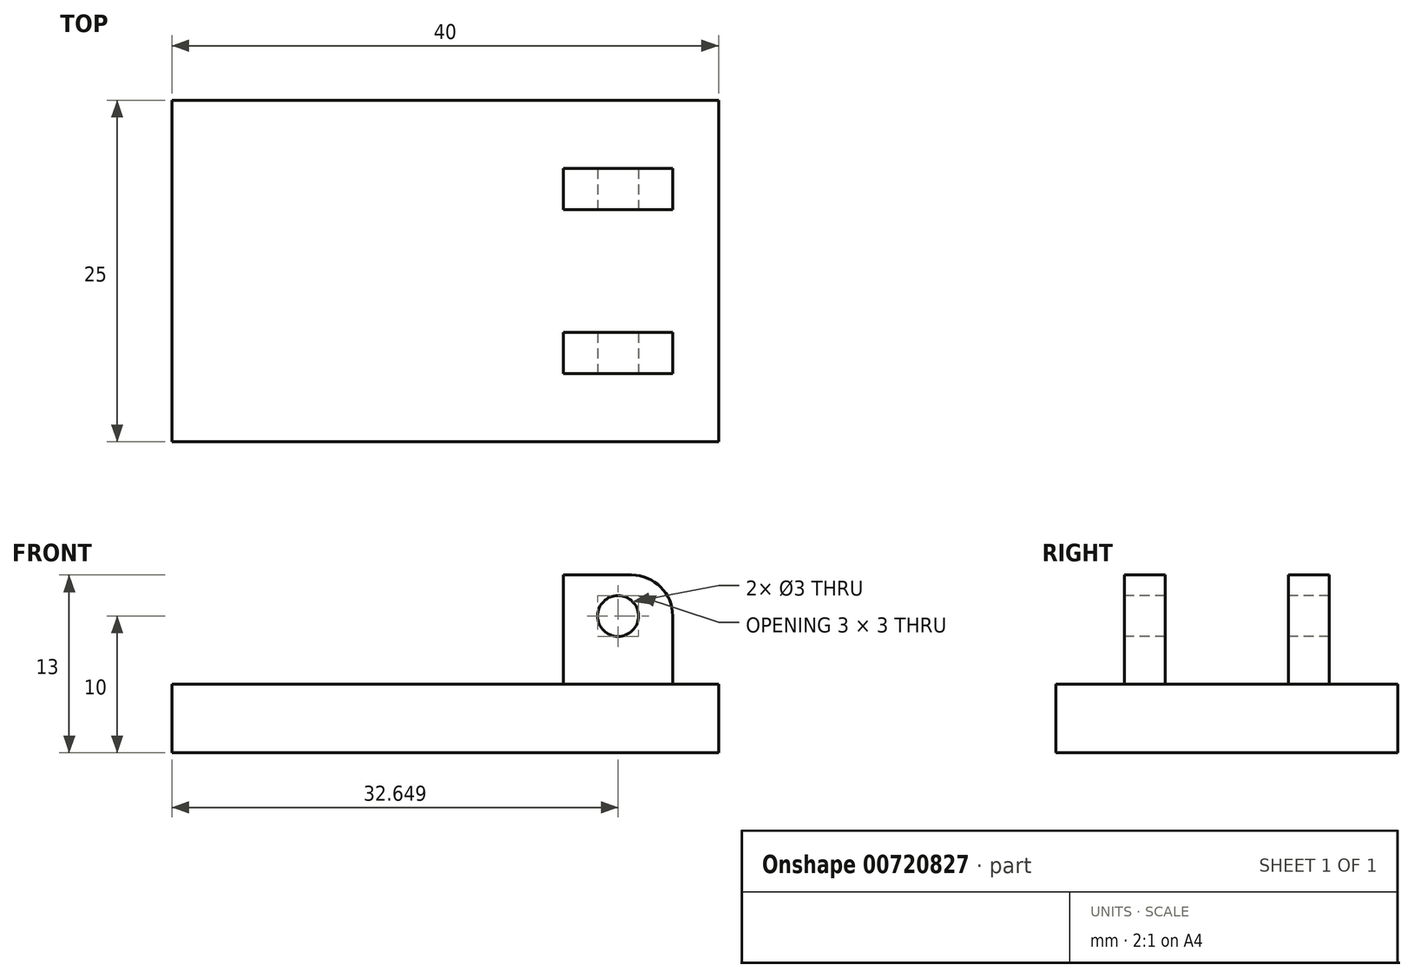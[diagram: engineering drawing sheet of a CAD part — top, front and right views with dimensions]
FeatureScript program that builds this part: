
annotation { "Feature Type Name" : "Feature", "Feature Type Description" : "" }
export const myFeature = defineFeature(function(context is Context, id is Id, definition is map)
    precondition{}
    {
        {
            var Q0;
            Q0=qCreatedBy(makeId("Top.planeOp"),FACE);
            var sketch = newSketch(context, id + "F0", { "sketchPlane" : qUnion([Q0])});
            skLineSegment(sketch, "E0.bottom", {"start": v(20, -12.5) * mm, "end": v(-20, -12.5) * mm});
            skLineSegment(sketch, "E0.top", {"start": v(20, 12.5) * mm, "end": v(-20, 12.5) * mm});
            skLineSegment(sketch, "E0.left", {"start": v(20, -12.5) * mm, "end": v(20, 12.5) * mm});
            skLineSegment(sketch, "E0.right", {"start": v(-20, -12.5) * mm, "end": v(-20, 12.5) * mm});
            skPoint(sketch, "E0.middle", {"position": v(0, 0) * mm});
            skSolve(sketch);
        }
        {
            var Q0;
            Q0=makeQuery(id+"F0.imprint","IMPRINT",FACE,{"disambiguationData":[TD([[makeQuery(id+"F0.imprint","IMPRINT",EDGE,{"derivedFrom":sQuery(id+"F0.wireOp",EDGE,"E0.bottom")}),-1.0]])]});
            extrude(context, id + "F1", {"entities" : qUnion([Q0]), "depth" : 5 * mm, "offsetDistance" : 25 * mm});
        }
        {
            var Q0;
            Q0=makeQuery(id+"F1.opExtrude","CAP_FACE",FACE,{"disambiguationData":[OSD([sQuery(id+"F0.wireOp",EDGE,"E0.bottom"),sQuery(id+"F0.wireOp",EDGE,"E0.top"),sQuery(id+"F0.wireOp",EDGE,"E0.left"),sQuery(id+"F0.wireOp",EDGE,"E0.right")])],"isStart":false});
            var sketch = newSketch(context, id + "F2", { "sketchPlane" : qUnion([Q0])});
            skLineSegment(sketch, "E1.bottom", {"start": v(16.65, -7.5) * mm, "end": v(8.65, -7.5) * mm});
            skLineSegment(sketch, "E1.top", {"start": v(16.65, 7.5) * mm, "end": v(8.65, 7.5) * mm});
            skLineSegment(sketch, "E1.right", {"start": v(8.65, -7.5) * mm, "end": v(8.65, 7.5) * mm});
            skPoint(sketch, "E1.middle", {"position": v(12.65, 0) * mm});
            skLineSegment(sketch, "E2", {"start": v(8.65, 7.5) * mm, "end": v(8.65, 4.5) * mm});
            skLineSegment(sketch, "E3", {"start": v(8.65, 4.5) * mm, "end": v(8.65, 1.5) * mm});
            skLineSegment(sketch, "E4", {"start": v(8.65, 1.5) * mm, "end": v(8.65, -1.5) * mm});
            skLineSegment(sketch, "E5", {"start": v(8.65, -1.5) * mm, "end": v(8.65, -4.5) * mm});
            skLineSegment(sketch, "E6", {"start": v(8.65, -4.5) * mm, "end": v(8.65, -7.5) * mm});
            skLineSegment(sketch, "E7", {"start": v(8.65, -7.5) * mm, "end": v(8.65, -4.5) * mm});
            skLineSegment(sketch, "E8", {"start": v(8.65, 4.5) * mm, "end": v(16.65, 4.5) * mm});
            skLineSegment(sketch, "E9", {"start": v(16.65, 4.5) * mm, "end": v(16.65, 1.5) * mm});
            skLineSegment(sketch, "E10", {"start": v(8.65, 1.5) * mm, "end": v(16.65, 1.5) * mm});
            skLineSegment(sketch, "E11", {"start": v(16.65, 1.5) * mm, "end": v(16.65, -1.5) * mm});
            skLineSegment(sketch, "E12", {"start": v(16.65, -1.5) * mm, "end": v(8.65, -1.5) * mm});
            skLineSegment(sketch, "E13.trimOffspring", {"start": v(16.65, -1.5) * mm, "end": v(16.65, 7.5) * mm});
            skLineSegment(sketch, "E14", {"start": v(16.65, -1.5) * mm, "end": v(16.65, -4.5) * mm});
            skLineSegment(sketch, "E15", {"start": v(16.65, -4.5) * mm, "end": v(16.65, -7.5) * mm});
            skLineSegment(sketch, "E16", {"start": v(8.65, -4.5) * mm, "end": v(16.65, -4.5) * mm});
            skSolve(sketch);
        }
        {
            var Q0;
            {var subQ0=sQuery(id+"F2.wireOp",EDGE,"E1.top");Q0=makeQuery(id+"F2.imprint","IMPRINT",FACE,{"disambiguationData":[TD([[makeQuery(id+"F2.imprint","IMPRINT",EDGE,{"derivedFrom":subQ0}),1.0]])]});}
            var Q1;
            Q1=makeQuery(id+"F2.imprint","IMPRINT",FACE,{"disambiguationData":[TD([[makeQuery(id+"F2.imprint","IMPRINT",EDGE,{"derivedFrom":sQuery(id+"F2.wireOp",EDGE,"E4")}),1.0]])]});
            var Q2;
            Q2=makeQuery(id+"F2.imprint","IMPRINT",FACE,{"disambiguationData":[TD([[makeQuery(id+"F2.imprint","IMPRINT",EDGE,{"derivedFrom":sQuery(id+"F2.wireOp",EDGE,"E1.bottom")}),-1.0]])]});
            extrude(context, id + "F3", {"entities" : qUnion([Q0, Q1, Q2]), "operationType" : NewBodyOperationType.ADD, "depth" : 8 * mm, "offsetDistance" : 25 * mm});
        }
        {
            var Q0;
            Q0=makeQuery(id+"F3.opExtrude","CAP_EDGE",EDGE,{"disambiguationData":[OSD([sQuery(id+"F2.wireOp",EDGE,"E7")])],"isStart":false});
            var Q1;
            Q1=makeQuery(id+"F3.opExtrude","CAP_EDGE",EDGE,{"disambiguationData":[OSD([sQuery(id+"F2.wireOp",EDGE,"E15")])],"isStart":false});
            var Q2;
            Q2=makeQuery(id+"F3.opExtrude","CAP_EDGE",EDGE,{"disambiguationData":[OSD([sQuery(id+"F2.wireOp",EDGE,"E4")])],"isStart":false});
            var Q3;
            {var subQ0=sQuery(id+"F2.wireOp",EDGE,"E13.trimOffspring");Q3=makeQuery(id+"F3.opExtrude","CAP_EDGE",EDGE,{"disambiguationData":[OSD([subQ0]),TDD([makeQuery(id+"F2.imprint","IMPRINT",EDGE,{"disambiguationData":[TD([[makeQuery(id+"F2.imprint","INTERSECT",VERTEX,{"derivedFrom":[sQuery(id+"F2.wireOp",EDGE,"E10"),subQ0]}),1.0]])],"derivedFrom":subQ0})])],"isStart":false});}
            var Q4;
            Q4=makeQuery(id+"F3.opExtrude","CAP_EDGE",EDGE,{"disambiguationData":[OSD([sQuery(id+"F2.wireOp",EDGE,"E2")])],"isStart":false});
            var Q5;
            {var subQ0=sQuery(id+"F2.wireOp",EDGE,"E13.trimOffspring");Q5=makeQuery(id+"F3.opExtrude","CAP_EDGE",EDGE,{"disambiguationData":[OSD([subQ0]),TDD([makeQuery(id+"F2.imprint","IMPRINT",EDGE,{"disambiguationData":[TD([[makeQuery(id+"F2.imprint","INTERSECT",VERTEX,{"derivedFrom":[sQuery(id+"F2.wireOp",EDGE,"E1.top"),subQ0]}),1.0]])],"derivedFrom":subQ0})])],"isStart":false});}
            fillet(context, id + "F4", {"entities" : qUnion([Q0, Q1, Q2, Q3, Q4, Q5]), "radius" : 3 * mm, "tangentPropagation" : true, "allowEdgeOverflow" : false});
        }
        {
            var Q0;
            Q0=makeQuery(id+"F3.opExtrude","SWEPT_FACE",FACE,{"disambiguationData":[OSD([sQuery(id+"F2.wireOp",EDGE,"E1.bottom")])]});
            var sketch = newSketch(context, id + "F5", { "sketchPlane" : qUnion([Q0])});
            skLineSegment(sketch, "E17", {"start": v(12.65, 13) * mm, "end": v(12.65, 10) * mm});
            skCircle(sketch, "E18", {"center": v(12.65, 10) * mm, "radius": 1.5 * mm});
            skSolve(sketch);
        }
        {
            var Q0;
            Q0=makeQuery(id+"F5.imprint","IMPRINT",FACE,{"disambiguationData":[TD([[makeQuery(id+"F5.imprint","IMPRINT",EDGE,{"derivedFrom":sQuery(id+"F5.wireOp",EDGE,"E18")}),1.0]])]});
            extrude(context, id + "F6", {"entities" : qUnion([Q0]), "operationType" : NewBodyOperationType.REMOVE, "oppositeDirection" : true, "depth" : 25 * mm, "offsetDistance" : 25 * mm});
        }
    });
